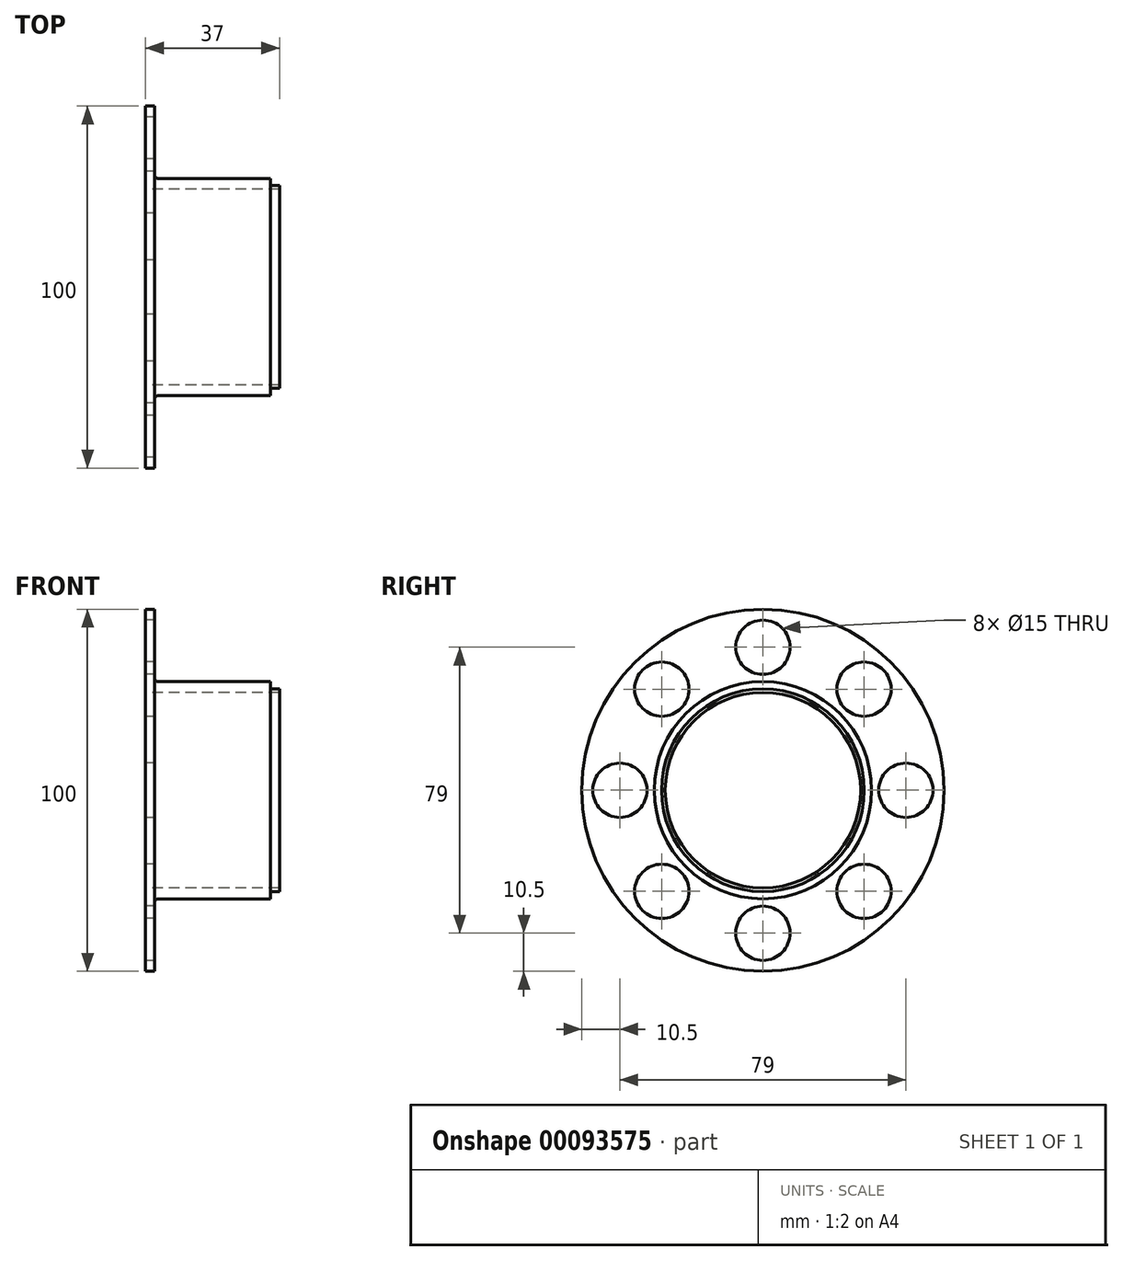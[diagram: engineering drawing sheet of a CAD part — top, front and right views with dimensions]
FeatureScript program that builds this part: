
annotation { "Feature Type Name" : "Feature", "Feature Type Description" : "" }
export const myFeature = defineFeature(function(context is Context, id is Id, definition is map)
    precondition{}
    {
        {
            var Q0;
            Q0=qCreatedBy(makeId("Top.planeOp"),FACE);
            var sketch = newSketch(context, id + "F0", { "sketchPlane" : qUnion([Q0])});
            skLineSegment(sketch, "E0", {"start": v(-38.03, 0) * mm, "end": v(48.17, 0) * mm, "construction": true});
            skLineSegment(sketch, "E1", {"start": v(0, 27) * mm, "end": v(-37, 27) * mm});
            skLineSegment(sketch, "E2", {"start": v(-37, 27) * mm, "end": v(-37, 50) * mm});
            skLineSegment(sketch, "E3", {"start": v(-37, 50) * mm, "end": v(-34.5, 50) * mm});
            skLineSegment(sketch, "E4", {"start": v(-34.5, 50) * mm, "end": v(-34.5, 30) * mm});
            skLineSegment(sketch, "E5", {"start": v(-34.5, 30) * mm, "end": v(-2.5, 30) * mm});
            skLineSegment(sketch, "E6", {"start": v(-2.5, 30) * mm, "end": v(-2.5, 50) * mm});
            skLineSegment(sketch, "E7", {"start": v(-2.5, 50) * mm, "end": v(0, 50) * mm});
            skLineSegment(sketch, "E8", {"start": v(0, 50) * mm, "end": v(0, 27) * mm});
            skSolve(sketch);
        }
        {
            var Q0;
            Q0=qSketchRegion(id+"F0",true);
            var Q1;
            Q1=sQuery(id+"F0.wireOp",EDGE,"E0");
            revolve(context, id + "F1", {"entities" : qUnion([Q0]), "axis" : qUnion([Q1]), "revolveType" : RevolveType.FULL});
        }
        {
            var Q0;
            Q0=makeQuery(id+"F1.opRevolve","SWEPT_FACE",FACE,{"disambiguationData":[OSD([sQuery(id+"F0.wireOp",EDGE,"E2")])]});
            var sketch = newSketch(context, id + "F2", { "sketchPlane" : qUnion([Q0])});
            skLineSegment(sketch, "E9", {"start": v(0, 0) * mm, "end": v(0, 39.5) * mm, "construction": true});
            skCircle(sketch, "E10", {"center": v(0, 39.5) * mm, "radius": 7.5 * mm});
            skCircle(sketch, "E11.1.0", {"center": v(-27.93, 27.93) * mm, "radius": 7.5 * mm});
            skCircle(sketch, "E11.2.0", {"center": v(-39.5, 0) * mm, "radius": 7.5 * mm});
            skCircle(sketch, "E11.3.0", {"center": v(-27.93, -27.93) * mm, "radius": 7.5 * mm});
            skCircle(sketch, "E11.4.0", {"center": v(0, -39.5) * mm, "radius": 7.5 * mm});
            skCircle(sketch, "E11.5.0", {"center": v(27.93, -27.93) * mm, "radius": 7.5 * mm});
            skCircle(sketch, "E11.6.0", {"center": v(39.5, 0) * mm, "radius": 7.5 * mm});
            skCircle(sketch, "E11.7.0", {"center": v(27.93, 27.93) * mm, "radius": 7.5 * mm});
            skPoint(sketch, "E11.center", {"position": v(0, 0) * mm});
            skSolve(sketch);
        }
        {
            var Q0;
            Q0 = qSketchRegion(id + "F2", true);
            extrude(context, id + "F3", {"entities" : qUnion([Q0]), "operationType" : NewBodyOperationType.REMOVE, "oppositeDirection" : true, "depth" : 5 * mm});
        }
        {
            var Q0;
            Q0=makeQuery(id+"F1.opRevolve","SWEPT_FACE",FACE,{"disambiguationData":[OSD([sQuery(id+"F0.wireOp",EDGE,"E8")])]});
            var sketch = newSketch(context, id + "F4", { "sketchPlane" : qUnion([Q0])});
            skCircle(sketch, "E12", {"center": v(0, 0) * mm, "radius": 55 * mm});
            skCircle(sketch, "E13", {"center": v(0, 0) * mm, "radius": 28 * mm});
            skSolve(sketch);
        }
        {
            var Q0;
            Q0 = qSketchRegion(id + "F4", true);
            extrude(context, id + "F5", {"entities" : qUnion([Q0]), "operationType" : NewBodyOperationType.REMOVE, "oppositeDirection" : true, "depth" : 2.5 * mm});
        }
        {
            var Q0;
            Q0=makeQuery(id+"F1.opRevolve","SWEPT_EDGE",EDGE,{"disambiguationData":[OSD([sQuery(id+"F0.wireOp",EDGE,"E4"),sQuery(id+"F0.wireOp",EDGE,"E5")])]});
            fillet(context, id + "F6", {"entities" : qUnion([Q0]), "radius" : 1 * mm, "tangentPropagation" : true, "allowEdgeOverflow" : false});
        }
    });
